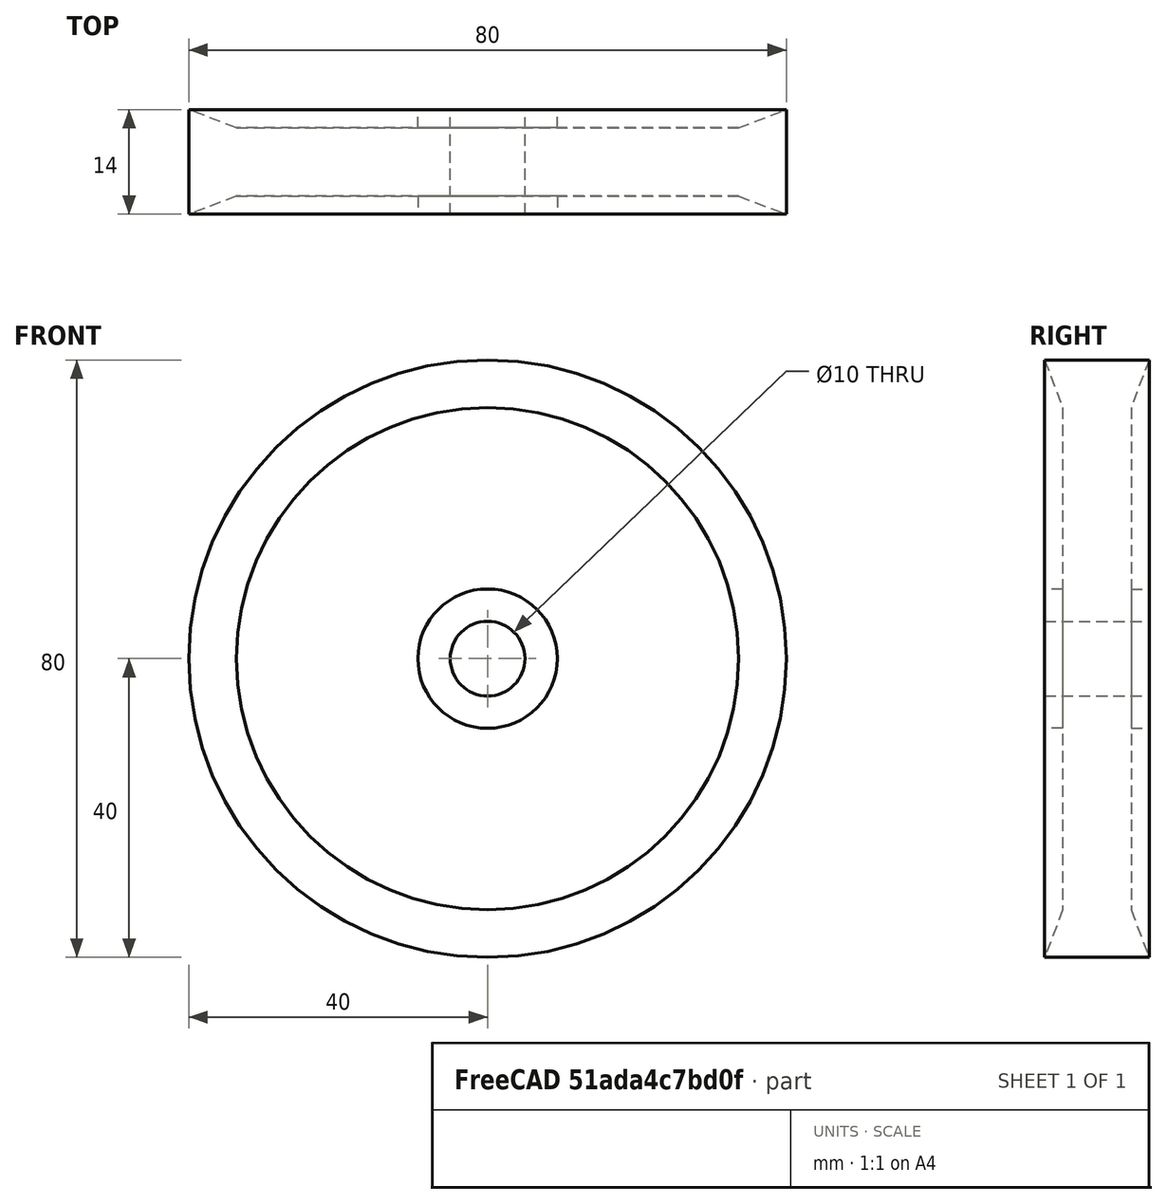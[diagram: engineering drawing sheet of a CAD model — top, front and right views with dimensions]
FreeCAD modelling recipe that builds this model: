
FCSTD DOCUMENT  (FreeCAD 0.16R6703 (Git))
Label: wheel_inside
License: Public Domain
LicenseURL: http://en.wikipedia.org/wiki/Public_domain
objects: Sketcher::SketchObject×1, PartDesign::Revolution×1
note: 3 computed .brp shape members not serialized (recipe doc carries the construction recipe); baked Part::Feature solids carry a one-line shape summary decoded from their .brp

FEATURE [Sketcher::SketchObject] Sketch  label="inside_sketch"
  Placement = pos=(0,0,0) rot=(0.57735,0.57735,0.57735;2.0944rad)
  sketch-geometry (19):
    g0: LineSegment [constr] StartX=-7 StartY=50 StartZ=0 EndX=7 EndY=50 EndZ=0
    g1: LineSegment [constr] StartX=7 StartY=50 StartZ=0 EndX=7 EndY=40 EndZ=0
    g2: LineSegment StartX=7 StartY=40 StartZ=0 EndX=-7 EndY=40 EndZ=0
    g3: LineSegment [constr] StartX=-7 StartY=40 StartZ=0 EndX=-7 EndY=50 EndZ=0
    g4: GeomPoint [constr] X=0 Y=45 Z=0
    g5: GeomPoint [constr] X=0 Y=50 Z=0
    g6: LineSegment StartX=-7 StartY=5 StartZ=0 EndX=7 EndY=5 EndZ=0
    g7: GeomPoint [constr] X=0 Y=5 Z=0
    g8: LineSegment [constr] StartX=-4.57259 StartY=33.6202 StartZ=0 EndX=4.57259 EndY=33.6202 EndZ=0
    g9: LineSegment StartX=4.57259 StartY=33.6202 StartZ=0 EndX=4.57259 EndY=9.33191 EndZ=0
    g10: LineSegment [constr] StartX=4.57259 StartY=9.33191 StartZ=0 EndX=-4.57259 EndY=9.33191 EndZ=0
    g11: LineSegment StartX=-4.57259 StartY=9.33191 StartZ=0 EndX=-4.57259 EndY=33.6202 EndZ=0
    g12: GeomPoint [constr] X=0 Y=21.4761 Z=0
    g13: LineSegment StartX=-7 StartY=40 StartZ=0 EndX=-4.57259 EndY=33.6202 EndZ=0
    g14: LineSegment StartX=7 StartY=40 StartZ=0 EndX=4.57259 EndY=33.6202 EndZ=0
    g15: LineSegment StartX=-4.57259 StartY=9.33191 StartZ=0 EndX=-7 EndY=9.33191 EndZ=0
    g16: LineSegment StartX=-7 StartY=5 StartZ=0 EndX=-7 EndY=9.33191 EndZ=0
    g17: LineSegment StartX=4.57259 StartY=9.33191 StartZ=0 EndX=7 EndY=9.33191 EndZ=0
    g18: LineSegment StartX=7 StartY=5 StartZ=0 EndX=7 EndY=9.33191 EndZ=0
  constraints (46):
    c: Coincident(g0,g1)
    c: Coincident(g1,g2)
    c: Coincident(g2,g3)
    c: Coincident(g3,g0)
    c: Horizontal(g0)
    c: Horizontal(g2)
    c: Vertical(g1)
    c: Vertical(g3)
    c: PointOnObject(g4,g-2)
    c: Symmetric(g0,g1,g4)
    c: DistanceY(g1,g1) = 10
    c: DistanceX(g0,g0) = 14
    c: PointOnObject(g5,g-2)
    c: PointOnObject(g5,g0)
    c: DistanceY(g-1,g5) = 50
    c: Horizontal(g6)
    c: PointOnObject(g7,g6)
    c: PointOnObject(g7,g-2)
    c: Symmetric(g6,g6,g7)
    c: DistanceY(g-1,g7) = 5
    c: Coincident(g8,g9)
    c: Coincident(g9,g10)
    c: Coincident(g10,g11)
    c: Coincident(g11,g8)
    c: Horizontal(g8)
    c: Horizontal(g10)
    c: Vertical(g9)
    c: Vertical(g11)
    c: PointOnObject(g12,g-2)
    c: Symmetric(g8,g9,g12)
    c: Coincident(g13,g2)
    c: Coincident(g13,g8)
    c: Coincident(g14,g1)
    c: Coincident(g14,g8)
    c: DistanceX(g6,g6) = 14
    c: DistanceX(g10,g10) = 9.14518
    c: Coincident(g15,g10)
    c: Horizontal(g15)
    c: Coincident(g16,g6)
    c: Coincident(g16,g15)
    c: Vertical(g16)
    c: Coincident(g17,g9)
    c: Horizontal(g17)
    c: Coincident(g18,g6)
    c: Coincident(g18,g17)
    c: Vertical(g18)
FEATURE [PartDesign::Revolution] Revolution
  Angle = 360
  Axis = (0,1,0)
  Base = (0,0,0)
  Placement = pos=(0,0,0) rot=(0.57735,0.57735,0.57735;2.0944rad)
  ReferenceAxis = -> Sketch [H_Axis]
  Sketch = -> Sketch
